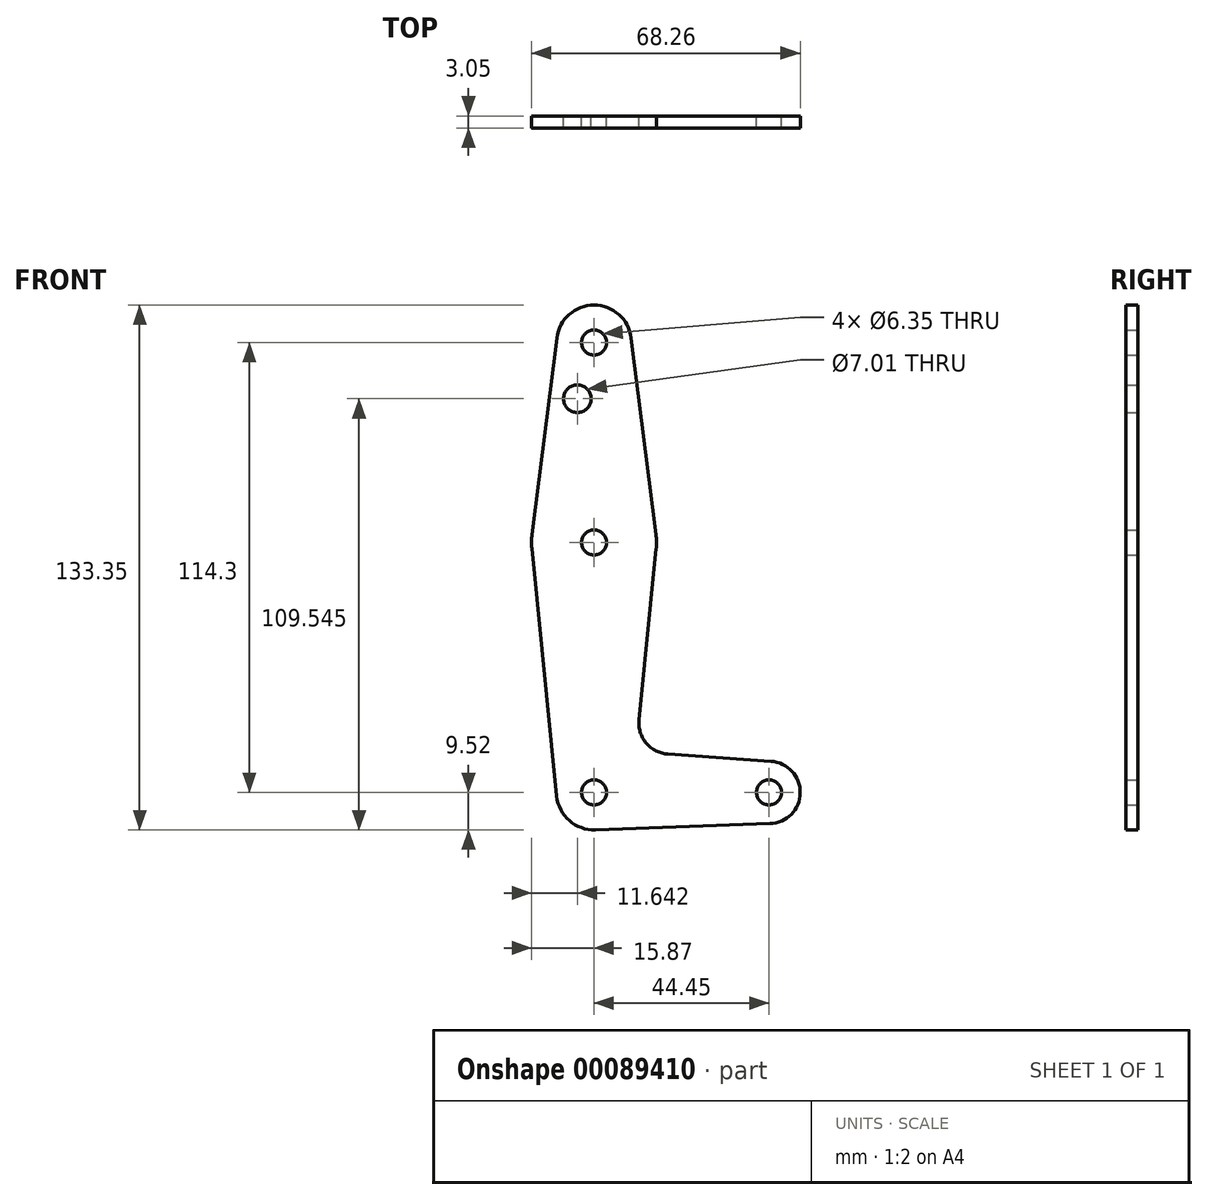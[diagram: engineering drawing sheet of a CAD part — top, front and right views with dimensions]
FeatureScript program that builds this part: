
annotation { "Feature Type Name" : "Feature", "Feature Type Description" : "" }
export const myFeature = defineFeature(function(context is Context, id is Id, definition is map)
    precondition{}
    {
        {
            var Q0;
            Q0=qCreatedBy(makeId("Front.planeOp"),FACE);
            var sketch = newSketch(context, id + "F0", { "sketchPlane" : qUnion([Q0])});
            skCircle(sketch, "E0", {"center": v(0, 114.3) * mm, "radius": 9.53 * mm});
            skCircle(sketch, "E1", {"center": v(0, 63.5) * mm, "radius": 15.88 * mm});
            skCircle(sketch, "E2", {"center": v(0, 0) * mm, "radius": 9.53 * mm});
            skCircle(sketch, "E3", {"center": v(44.45, 0) * mm, "radius": 7.94 * mm});
            skLineSegment(sketch, "E4", {"start": v(0, 114.3) * mm, "end": v(0, 0) * mm, "construction": true});
            skLineSegment(sketch, "E5", {"start": v(0, 0) * mm, "end": v(44.45, 0) * mm, "construction": true});
            skLineSegment(sketch, "E6", {"start": v(9.45, 115.5) * mm, "end": v(15.75, 65.48) * mm});
            skLineSegment(sketch, "E7", {"start": v(15.8, 61.91) * mm, "end": v(11.43, 18.44) * mm});
            skLineSegment(sketch, "E8", {"start": v(-15.8, 61.91) * mm, "end": v(-9.48, -0.95) * mm});
            skLineSegment(sketch, "E9", {"start": v(18.8, 9.72) * mm, "end": v(45, 7.92) * mm});
            skLineSegment(sketch, "E10", {"start": v(0.34, -9.52) * mm, "end": v(44.73, -7.93) * mm});
            skCircle(sketch, "E11", {"center": v(-4.23, 100.03) * mm, "radius": 3.5 * mm});
            skCircle(sketch, "E12.0", {"center": v(0, 114.3) * mm, "radius": 3.17 * mm});
            skCircle(sketch, "E13", {"center": v(0, 63.5) * mm, "radius": 3.17 * mm});
            skCircle(sketch, "E14", {"center": v(0, 0) * mm, "radius": 3.17 * mm});
            skCircle(sketch, "E15", {"center": v(44.45, 0) * mm, "radius": 3.17 * mm});
            skArc(sketch, "E16.filletArc", {"start": v(11.43, 18.44) * mm, "mid": v(13.26, 12.52) * mm, "end": v(18.8, 9.72) * mm});
            skLineSegment(sketch, "E17", {"start": v(-15.75, 65.48) * mm, "end": v(-9.45, 115.5) * mm});
            skSolve(sketch);
        }
        {
            var Q0;
            Q0 = qSketchRegion(id + "F0", true);
            extrude(context, id + "F1", {"entities" : qUnion([Q0]), "depth" : 3.05 * mm});
        }
    });
